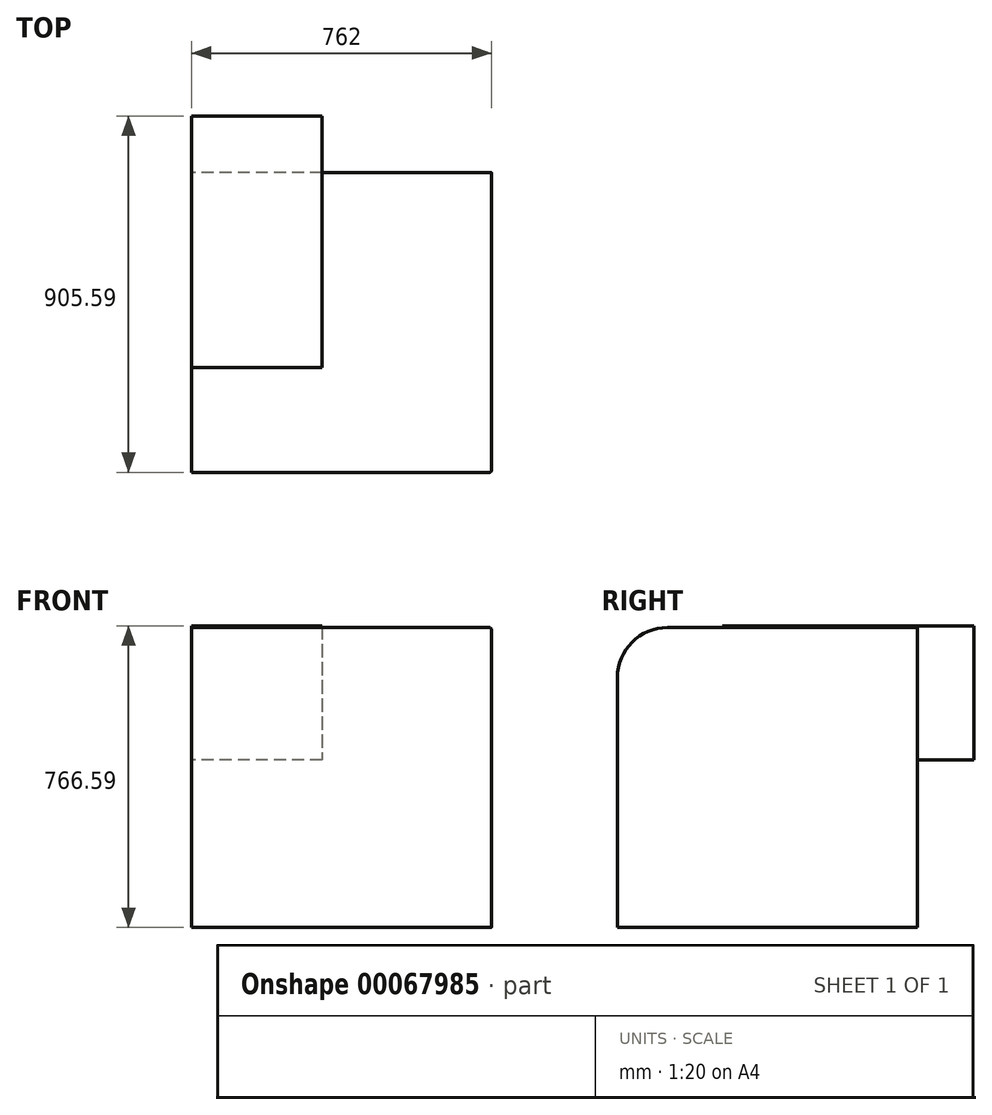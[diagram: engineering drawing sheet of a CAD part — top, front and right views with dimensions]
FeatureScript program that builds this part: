
annotation { "Feature Type Name" : "Feature", "Feature Type Description" : "" }
export const myFeature = defineFeature(function(context is Context, id is Id, definition is map)
    precondition{}
    {
        {
            var Q0;
            Q0=qCreatedBy(makeId("Front.planeOp"),FACE);
            var sketch = newSketch(context, id + "F0", { "sketchPlane" : qUnion([Q0])});
            skLineSegment(sketch, "E0.bottom", {"start": v(-508, 508) * mm, "end": v(254, 508) * mm});
            skLineSegment(sketch, "E0.top", {"start": v(-508, -254) * mm, "end": v(254, -254) * mm});
            skLineSegment(sketch, "E0.left", {"start": v(-508, 508) * mm, "end": v(-508, -254) * mm});
            skLineSegment(sketch, "E0.right", {"start": v(254, 508) * mm, "end": v(254, -254) * mm});
            skSolve(sketch);
        }
        {
            var Q0;
            Q0=makeQuery(id+"F0.imprint","IMPRINT",FACE,{"disambiguationData":[TD([[makeQuery(id+"F0.imprint","IMPRINT",EDGE,{"derivedFrom":sQuery(id+"F0.wireOp",EDGE,"E0.bottom")}),-1.0]])]});
            extrude(context, id + "F1", {"entities" : qUnion([Q0]), "depth" : 762 * mm});
        }
        {
            var Q0;
            Q0=makeQuery(id+"F1.opExtrude","CAP_EDGE",EDGE,{"disambiguationData":[OSD([sQuery(id+"F0.wireOp",EDGE,"E0.bottom")])],"isStart":false});
            fillet(context, id + "F2", {"entities" : qUnion([Q0]), "radius" : 127 * mm, "tangentPropagation" : true, "allowEdgeOverflow" : false});
        }
        {
            var Q0;
            Q0=makeQuery(id+"F1.opExtrude","SWEPT_FACE",FACE,{"disambiguationData":[OSD([sQuery(id+"F0.wireOp",EDGE,"E0.left")])]});
            var sketch = newSketch(context, id + "F3", { "sketchPlane" : qUnion([Q0])});
            skLineSegment(sketch, "E1.bottom", {"start": v(-143.6, 512.6) * mm, "end": v(495.5, 512.6) * mm});
            skLineSegment(sketch, "E1.top", {"start": v(-143.6, 172.3) * mm, "end": v(495.5, 172.3) * mm});
            skLineSegment(sketch, "E1.left", {"start": v(-143.6, 512.6) * mm, "end": v(-143.6, 172.3) * mm});
            skLineSegment(sketch, "E1.right", {"start": v(495.5, 512.6) * mm, "end": v(495.5, 172.3) * mm});
            skSolve(sketch);
        }
        {
            var Q0;
            {var subQ2=sQuery(id+"F3.wireOp",EDGE,"E1.bottom");Q0=makeQuery(id+"F3.imprint","IMPRINT",FACE,{"disambiguationData":[TD([[makeQuery(id+"F3.imprint","IMPRINT",EDGE,{"derivedFrom":subQ2}),-1.0]])]});}
            extrude(context, id + "F4", {"entities" : qUnion([Q0]), "oppositeDirection" : true, "depth" : 331.6 * mm});
        }
        {
            var Q0;
            Q0=makeQuery(id+"F1.opExtrude","CAP_EDGE",EDGE,{"disambiguationData":[OSD([sQuery(id+"F0.wireOp",EDGE,"E0.right")])],"isStart":false});
            fillet(context, id + "F5", {"entities" : qUnion([Q0]), "radius" : 5.08 * mm, "tangentPropagation" : true, "allowEdgeOverflow" : false});
        }
    });
